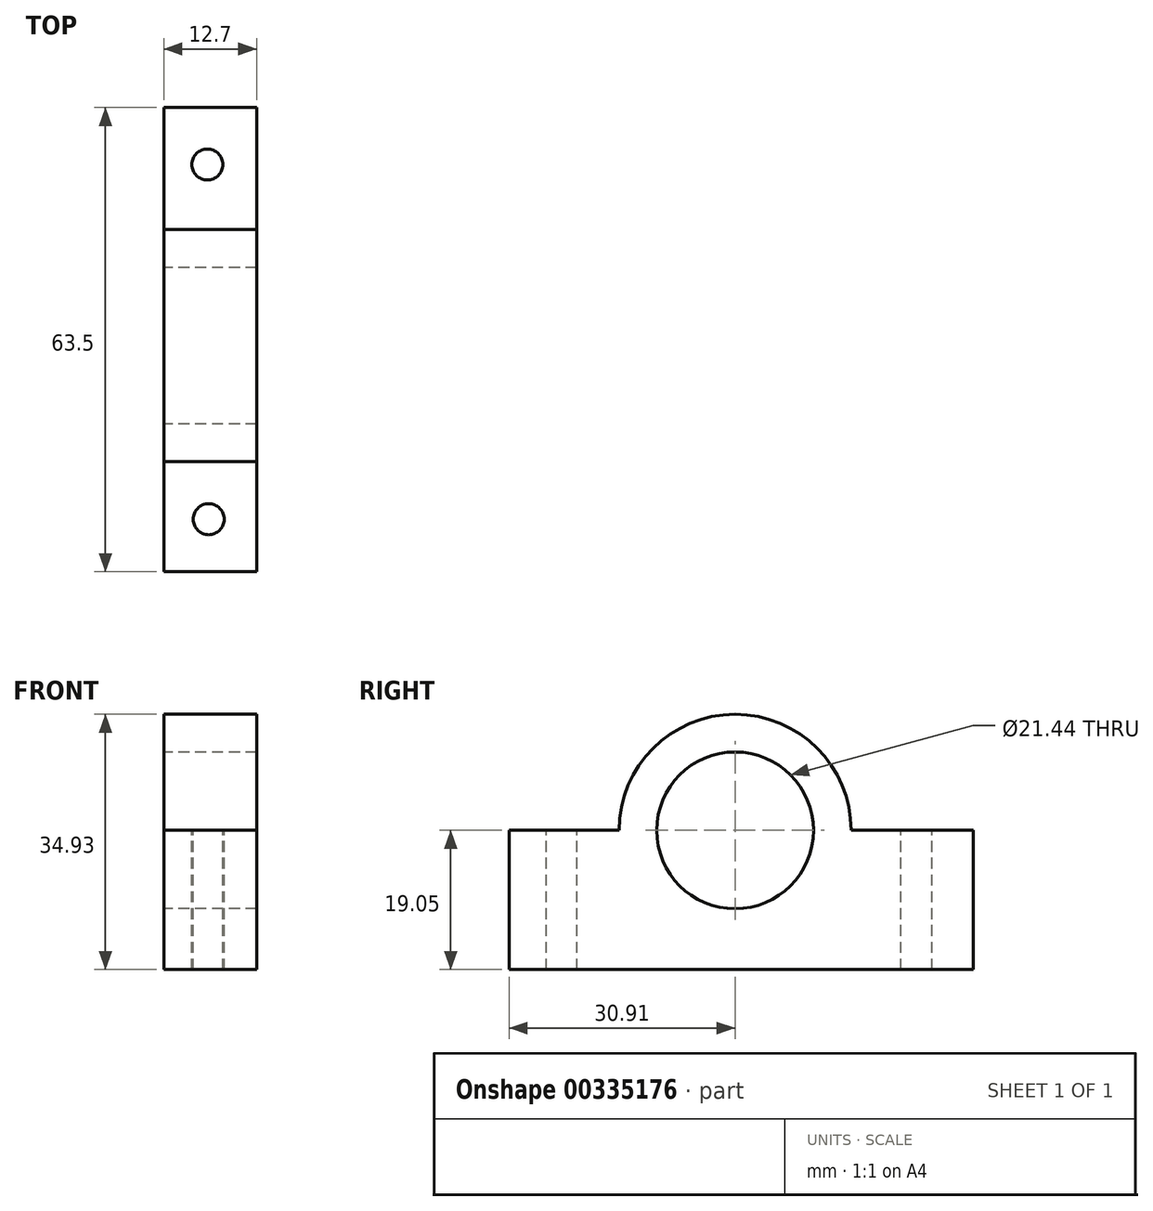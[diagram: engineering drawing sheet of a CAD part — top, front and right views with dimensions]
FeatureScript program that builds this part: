
annotation { "Feature Type Name" : "Feature", "Feature Type Description" : "" }
export const myFeature = defineFeature(function(context is Context, id is Id, definition is map)
    precondition{}
    {
        {
            var Q0;
            Q0=qCreatedBy(makeId("Right.planeOp"),FACE);
            var sketch = newSketch(context, id + "F0", { "sketchPlane" : qUnion([Q0])});
            skCircle(sketch, "E0", {"center": v(0, 0) * mm, "radius": 15.88 * mm});
            skCircle(sketch, "E1", {"center": v(0, 0) * mm, "radius": 10.72 * mm});
            skLineSegment(sketch, "E2.bottom", {"start": v(-30.9, 0) * mm, "end": v(32.6, 0) * mm});
            skLineSegment(sketch, "E2.top", {"start": v(-30.9, -19.05) * mm, "end": v(32.6, -19.05) * mm});
            skLineSegment(sketch, "E2.left", {"start": v(-30.9, 0) * mm, "end": v(-30.9, -19.05) * mm});
            skLineSegment(sketch, "E2.right", {"start": v(32.6, 0) * mm, "end": v(32.6, -19.05) * mm});
            skSolve(sketch);
        }
        {
            var Q0;
            Q0 = qSketchRegion(id + "F0", true);
            extrude(context, id + "F1", {"entities" : qUnion([Q0]), "depth" : 12.7 * mm});
        }
        {
            var Q0;
            {var subQ0=sQuery(id+"F0.wireOp",EDGE,"E2.bottom");Q0=makeQuery(id+"F1.opExtrude","SWEPT_FACE",FACE,{"disambiguationData":[OSD([subQ0]),TDD([makeQuery(id+"F0.imprint","IMPRINT",EDGE,{"disambiguationData":[TD([[makeQuery(id+"F0.imprint","INTERSECT",VERTEX,{"derivedFrom":[subQ0,sQuery(id+"F0.wireOp",EDGE,"E2.left")]}),-1.0]])],"derivedFrom":subQ0})])]});}
            var sketch = newSketch(context, id + "F2", { "sketchPlane" : qUnion([Q0])});
            skCircle(sketch, "E3", {"center": v(5.96, 24.8) * mm, "radius": 2.12 * mm});
            skSolve(sketch);
        }
        {
            var Q0;
            Q0 = qSketchRegion(id + "F2", true);
            extrude(context, id + "F3", {"entities" : qUnion([Q0]), "operationType" : NewBodyOperationType.REMOVE, "oppositeDirection" : true, "depth" : 25.4 * mm});
        }
        {
            var Q0;
            {var subQ0=sQuery(id+"F0.wireOp",EDGE,"E2.bottom");Q0=makeQuery(id+"F1.opExtrude","SWEPT_FACE",FACE,{"disambiguationData":[OSD([subQ0]),TDD([makeQuery(id+"F0.imprint","IMPRINT",EDGE,{"disambiguationData":[TD([[makeQuery(id+"F0.imprint","INTERSECT",VERTEX,{"derivedFrom":[subQ0,sQuery(id+"F0.wireOp",EDGE,"E2.left")]}),-1.0]])],"derivedFrom":subQ0})])]});}
            var sketch = newSketch(context, id + "F4", { "sketchPlane" : qUnion([Q0])});
            skCircle(sketch, "E4", {"center": v(6.14, -23.73) * mm, "radius": 2.12 * mm});
            skSolve(sketch);
        }
        {
            var Q0;
            Q0 = qSketchRegion(id + "F4", true);
            extrude(context, id + "F5", {"entities" : qUnion([Q0]), "operationType" : NewBodyOperationType.REMOVE, "oppositeDirection" : true, "depth" : 25.4 * mm});
        }
    });
